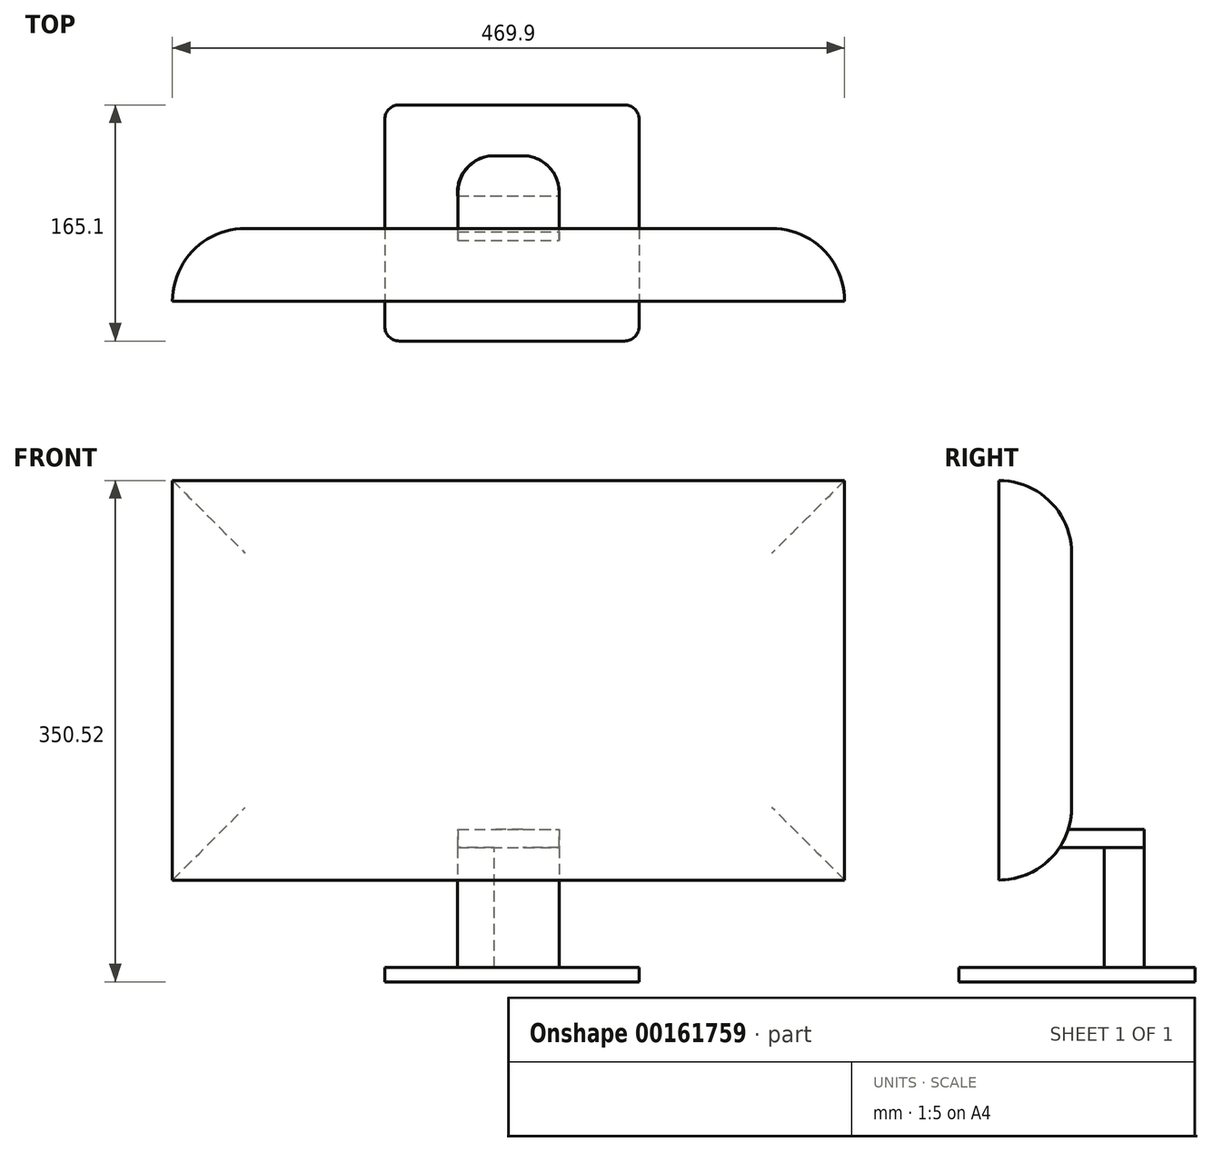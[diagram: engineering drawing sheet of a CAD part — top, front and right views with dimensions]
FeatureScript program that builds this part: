
annotation { "Feature Type Name" : "Feature", "Feature Type Description" : "" }
export const myFeature = defineFeature(function(context is Context, id is Id, definition is map)
    precondition{}
    {
        {
            var Q0;
            Q0=qCreatedBy(makeId("Top.planeOp"),FACE);
            var sketch = newSketch(context, id + "F0", { "sketchPlane" : qUnion([Q0])});
            skLineSegment(sketch, "E0.bottom", {"start": v(-33.52, 128.59) * mm, "end": v(144.28, 128.59) * mm});
            skLineSegment(sketch, "E0.top", {"start": v(-33.52, -36.51) * mm, "end": v(144.28, -36.51) * mm});
            skLineSegment(sketch, "E0.left", {"start": v(-33.52, 128.59) * mm, "end": v(-33.52, -36.51) * mm});
            skLineSegment(sketch, "E0.right", {"start": v(144.28, 128.59) * mm, "end": v(144.28, -36.51) * mm});
            skSolve(sketch);
        }
        {
            var Q0;
            Q0 = qSketchRegion(id + "F0", true);
            extrude(context, id + "F1", {"entities" : qUnion([Q0]), "depth" : 10.16 * mm});
        }
        {
            var Q0;
            Q0=makeQuery(id+"F1.opExtrude","SWEPT_EDGE",EDGE,{"disambiguationData":[OSD([sQuery(id+"F0.wireOp",EDGE,"E0.top"),sQuery(id+"F0.wireOp",EDGE,"E0.left")])]});
            var Q1;
            Q1=makeQuery(id+"F1.opExtrude","SWEPT_EDGE",EDGE,{"disambiguationData":[OSD([sQuery(id+"F0.wireOp",EDGE,"E0.bottom"),sQuery(id+"F0.wireOp",EDGE,"E0.left")])]});
            var Q2;
            Q2=makeQuery(id+"F1.opExtrude","SWEPT_EDGE",EDGE,{"disambiguationData":[OSD([sQuery(id+"F0.wireOp",EDGE,"E0.top"),sQuery(id+"F0.wireOp",EDGE,"E0.right")])]});
            var Q3;
            Q3=makeQuery(id+"F1.opExtrude","SWEPT_EDGE",EDGE,{"disambiguationData":[OSD([sQuery(id+"F0.wireOp",EDGE,"E0.bottom"),sQuery(id+"F0.wireOp",EDGE,"E0.right")])]});
            fillet(context, id + "F2", {"entities" : qUnion([Q0, Q1, Q2, Q3]), "radius" : 10.16 * mm, "tangentPropagation" : true, "allowEdgeOverflow" : false});
        }
        {
            var Q0;
            Q0=makeQuery(id+"F1.opExtrude","CAP_FACE",FACE,{"disambiguationData":[OSD([sQuery(id+"F0.wireOp",EDGE,"E0.bottom"),sQuery(id+"F0.wireOp",EDGE,"E0.top"),sQuery(id+"F0.wireOp",EDGE,"E0.left"),sQuery(id+"F0.wireOp",EDGE,"E0.right")])],"isStart":false});
            var sketch = newSketch(context, id + "F3", { "sketchPlane" : qUnion([Q0])});
            skLineSegment(sketch, "E1.bottom", {"start": v(42.68, 93.03) * mm, "end": v(63, 93.03) * mm});
            skLineSegment(sketch, "E1.top", {"start": v(17.28, 65.09) * mm, "end": v(88.4, 65.09) * mm});
            skLineSegment(sketch, "E1.left", {"start": v(17.28, 67.63) * mm, "end": v(17.28, 65.09) * mm});
            skLineSegment(sketch, "E1.right", {"start": v(88.4, 67.63) * mm, "end": v(88.4, 65.09) * mm});
            skPoint(sketch, "E2.visualSharp", {"position": v(17.28, 93.03) * mm});
            skArc(sketch, "E2.filletArc", {"start": v(42.68, 93.03) * mm, "mid": v(24.72, 85.59) * mm, "end": v(17.28, 67.63) * mm});
            skPoint(sketch, "E3.visualSharp", {"position": v(88.4, 93.03) * mm});
            skArc(sketch, "E3.filletArc", {"start": v(88.4, 67.63) * mm, "mid": v(80.96, 85.59) * mm, "end": v(63, 93.03) * mm});
            skSolve(sketch);
        }
        {
            var Q0;
            Q0 = qSketchRegion(id + "F3", true);
            extrude(context, id + "F4", {"entities" : qUnion([Q0]), "operationType" : NewBodyOperationType.ADD, "depth" : 83.82 * mm});
        }
        {
            var Q0;
            Q0=makeQuery(id+"F4.opExtrude","SWEPT_FACE",FACE,{"disambiguationData":[OSD([sQuery(id+"F3.wireOp",EDGE,"E1.bottom")])]});
            var sketch = newSketch(context, id + "F5", { "sketchPlane" : qUnion([Q0])});
            skLineSegment(sketch, "E4.bottom", {"start": v(-88.25, 93.98) * mm, "end": v(-17.75, 93.98) * mm});
            skLineSegment(sketch, "E4.top", {"start": v(-88.25, 106.68) * mm, "end": v(-17.75, 106.68) * mm});
            skLineSegment(sketch, "E4.left", {"start": v(-88.25, 93.98) * mm, "end": v(-88.25, 106.68) * mm});
            skLineSegment(sketch, "E4.right", {"start": v(-17.75, 93.98) * mm, "end": v(-17.75, 106.68) * mm});
            skSolve(sketch);
        }
        {
            var Q0;
            Q0 = qSketchRegion(id + "F5", true);
            extrude(context, id + "F6", {"entities" : qUnion([Q0]), "operationType" : NewBodyOperationType.ADD, "oppositeDirection" : true, "depth" : 50.8 * mm});
        }
        {
            var Q0;
            Q0=makeQuery(id+"F6.opExtrude","CAP_EDGE",EDGE,{"disambiguationData":[OSD([sQuery(id+"F5.wireOp",EDGE,"E4.right")])],"isStart":true});
            var Q1;
            Q1=makeQuery(id+"F6.opExtrude","CAP_EDGE",EDGE,{"disambiguationData":[OSD([sQuery(id+"F5.wireOp",EDGE,"E4.left")])],"isStart":true});
            fillet(context, id + "F7", {"entities" : qUnion([Q0, Q1]), "radius" : 25.4 * mm, "tangentPropagation" : true, "allowEdgeOverflow" : false});
        }
        {
            var Q0;
            Q0=makeQuery(id+"F6.opExtrude","CAP_FACE",FACE,{"disambiguationData":[OSD([sQuery(id+"F5.wireOp",EDGE,"E4.bottom"),sQuery(id+"F5.wireOp",EDGE,"E4.top"),sQuery(id+"F5.wireOp",EDGE,"E4.left"),sQuery(id+"F5.wireOp",EDGE,"E4.right")])],"isStart":false});
            var sketch = newSketch(context, id + "F8", { "sketchPlane" : qUnion([Q0])});
            skLineSegment(sketch, "E5.bottom", {"start": v(-181.95, 350.52) * mm, "end": v(287.95, 350.52) * mm});
            skLineSegment(sketch, "E5.top", {"start": v(-181.95, 71.12) * mm, "end": v(287.95, 71.12) * mm});
            skLineSegment(sketch, "E5.left", {"start": v(-181.95, 350.52) * mm, "end": v(-181.95, 71.12) * mm});
            skLineSegment(sketch, "E5.right", {"start": v(287.95, 350.52) * mm, "end": v(287.95, 71.12) * mm});
            skPoint(sketch, "E6", {"position": v(53, 350.52) * mm});
            skPoint(sketch, "E7", {"position": v(53, 93.98) * mm});
            skSolve(sketch);
        }
        {
            var Q0;
            Q0 = qSketchRegion(id + "F8", true);
            extrude(context, id + "F9", {"entities" : qUnion([Q0]), "operationType" : NewBodyOperationType.ADD, "depth" : 50.8 * mm});
        }
        {
            var Q0;
            Q0=makeQuery(id+"F9.opExtrude","CAP_EDGE",EDGE,{"disambiguationData":[OSD([sQuery(id+"F8.wireOp",EDGE,"E5.left")])],"isStart":true});
            var Q1;
            Q1=makeQuery(id+"F9.opExtrude","CAP_EDGE",EDGE,{"disambiguationData":[OSD([sQuery(id+"F8.wireOp",EDGE,"E5.right")])],"isStart":true});
            var Q2;
            Q2=makeQuery(id+"F9.opExtrude","CAP_EDGE",EDGE,{"disambiguationData":[OSD([sQuery(id+"F8.wireOp",EDGE,"E5.bottom")])],"isStart":true});
            var Q3;
            Q3=makeQuery(id+"F9.opExtrude","CAP_EDGE",EDGE,{"disambiguationData":[OSD([sQuery(id+"F8.wireOp",EDGE,"E5.top")])],"isStart":true});
            fillet(context, id + "F10", {"entities" : qUnion([Q0, Q1, Q2, Q3]), "radius" : 50.8 * mm, "tangentPropagation" : true, "allowEdgeOverflow" : false});
        }
    });
